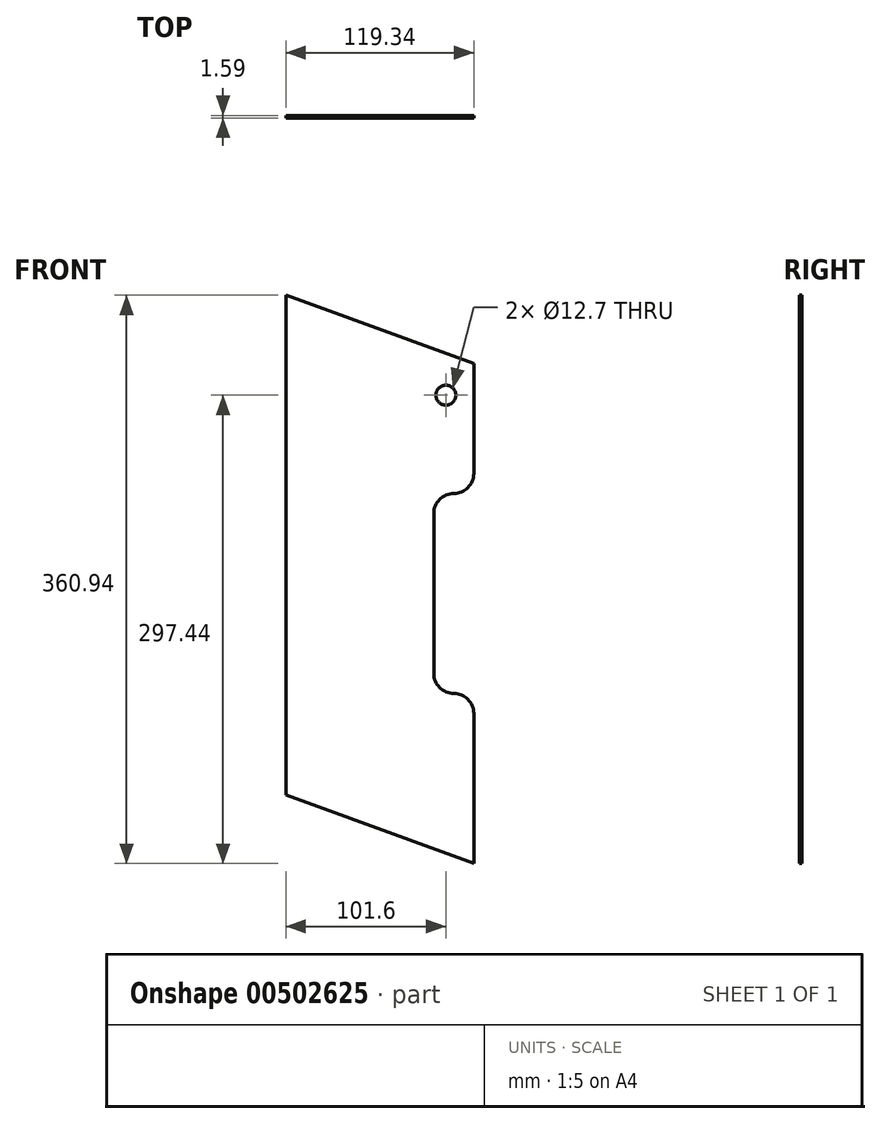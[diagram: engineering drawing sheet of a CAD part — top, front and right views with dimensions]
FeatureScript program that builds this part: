
annotation { "Feature Type Name" : "Feature", "Feature Type Description" : "" }
export const myFeature = defineFeature(function(context is Context, id is Id, definition is map)
    precondition{}
    {
        {
            var Q0;
            Q0=qCreatedBy(makeId("Front.planeOp"),FACE);
            var sketch = newSketch(context, id + "F0", { "sketchPlane" : qUnion([Q0])});
            skLineSegment(sketch, "E0.bottom", {"start": v(0, 0) * mm, "end": v(119.34, -43.44) * mm});
            skLineSegment(sketch, "E0.top", {"start": v(0, 317.5) * mm, "end": v(119.34, 274.06) * mm});
            skLineSegment(sketch, "E0.left", {"start": v(0, 0) * mm, "end": v(0, 317.5) * mm});
            skLineSegment(sketch, "E0.right", {"start": v(119.34, -43.44) * mm, "end": v(119.34, 51.81) * mm});
            skCircle(sketch, "E1", {"center": v(101.6, 254) * mm, "radius": 6.35 * mm});
            skLineSegment(sketch, "E2.trimOffspring", {"start": v(119.34, 274.06) * mm, "end": v(119.34, 274.06) * mm});
            skLineSegment(sketch, "E3.bottom", {"start": v(106.64, 191.51) * mm, "end": v(106.64, 191.51) * mm});
            skLineSegment(sketch, "E3.top", {"start": v(106.64, 64.51) * mm, "end": v(106.64, 64.51) * mm});
            skLineSegment(sketch, "E3.right", {"start": v(93.94, 178.81) * mm, "end": v(93.94, 77.21) * mm});
            skPoint(sketch, "E4.visualSharp", {"position": v(93.94, 191.51) * mm});
            skArc(sketch, "E4.filletArc", {"start": v(106.64, 191.51) * mm, "mid": v(97.66, 187.8) * mm, "end": v(93.94, 178.81) * mm});
            skPoint(sketch, "E5.visualSharp", {"position": v(93.94, 64.51) * mm});
            skArc(sketch, "E5.filletArc", {"start": v(93.94, 77.21) * mm, "mid": v(97.66, 68.23) * mm, "end": v(106.64, 64.51) * mm});
            skPoint(sketch, "E6", {"position": v(119.34, 274.06) * mm});
            skLineSegment(sketch, "E7.trimOffspring", {"start": v(119.34, 204.21) * mm, "end": v(119.34, 274.06) * mm});
            skPoint(sketch, "E8.visualSharp", {"position": v(119.34, 191.51) * mm});
            skArc(sketch, "E8.filletArc", {"start": v(106.64, 191.51) * mm, "mid": v(115.62, 195.23) * mm, "end": v(119.34, 204.21) * mm});
            skPoint(sketch, "E9.visualSharp", {"position": v(119.34, 64.51) * mm});
            skArc(sketch, "E9.filletArc", {"start": v(119.34, 51.81) * mm, "mid": v(115.62, 60.8) * mm, "end": v(106.64, 64.51) * mm});
            skSolve(sketch);
        }
        {
            var Q0;
            Q0=makeQuery(id+"F0.imprint","IMPRINT",FACE,{"disambiguationData":[TD([[makeQuery(id+"F0.imprint","IMPRINT",EDGE,{"derivedFrom":sQuery(id+"F0.wireOp",EDGE,"E0.bottom")}),1.0]])]});
            extrude(context, id + "F1", {"entities" : qUnion([Q0]), "depth" : 1.59 * mm});
        }
    });
